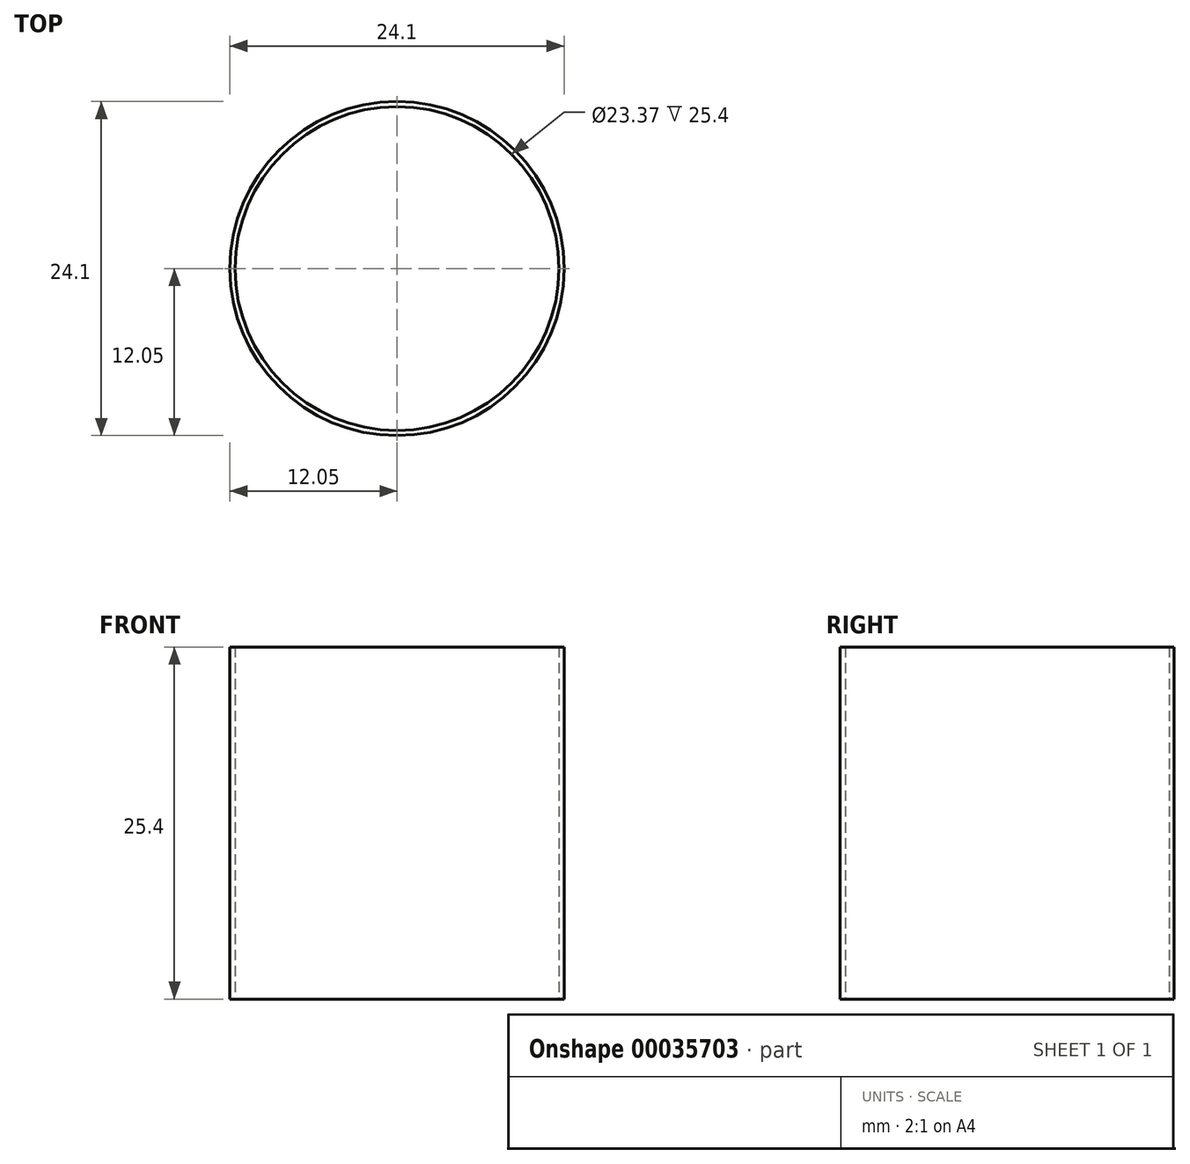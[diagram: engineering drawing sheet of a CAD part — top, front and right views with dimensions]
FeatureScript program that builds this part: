
annotation { "Feature Type Name" : "Feature", "Feature Type Description" : "" }
export const myFeature = defineFeature(function(context is Context, id is Id, definition is map)
    precondition{}
    {
        {
            var Q0;
            Q0=qCreatedBy(makeId("Front.planeOp"),FACE);
            var sketch = newSketch(context, id + "F0", { "sketchPlane" : qUnion([Q0])});
            skLineSegment(sketch, "E0", {"start": v(0, 0) * mm, "end": v(0, 25.4) * mm});
            skLineSegment(sketch, "E1", {"start": v(0, 25.4) * mm, "end": v(12.05, 25.4) * mm});
            skLineSegment(sketch, "E2", {"start": v(12.05, 25.4) * mm, "end": v(12.05, 0) * mm});
            skLineSegment(sketch, "E3", {"start": v(12.05, 0) * mm, "end": v(0, 0) * mm});
            skLineSegment(sketch, "E4", {"start": v(11.68, 0) * mm, "end": v(12.05, 0) * mm});
            skLineSegment(sketch, "E5", {"start": v(11.68, 0) * mm, "end": v(11.68, 25.4) * mm});
            skLineSegment(sketch, "E6", {"start": v(12.05, 25.4) * mm, "end": v(11.68, 25.4) * mm});
            skSolve(sketch);
        }
        {
            var Q0;
            Q0=makeQuery(id+"F0.imprint","IMPRINT",FACE,{"disambiguationData":[TD([[makeQuery(id+"F0.imprint","IMPRINT",EDGE,{"derivedFrom":sQuery(id+"F0.wireOp",EDGE,"E2")}),-1.0]])]});
            var Q1;
            Q1=sQuery(id+"F0.wireOp",EDGE,"E0");
            revolve(context, id + "F1", {"entities" : qUnion([Q0]), "axis" : qUnion([Q1]), "revolveType" : RevolveType.FULL});
        }
    });
